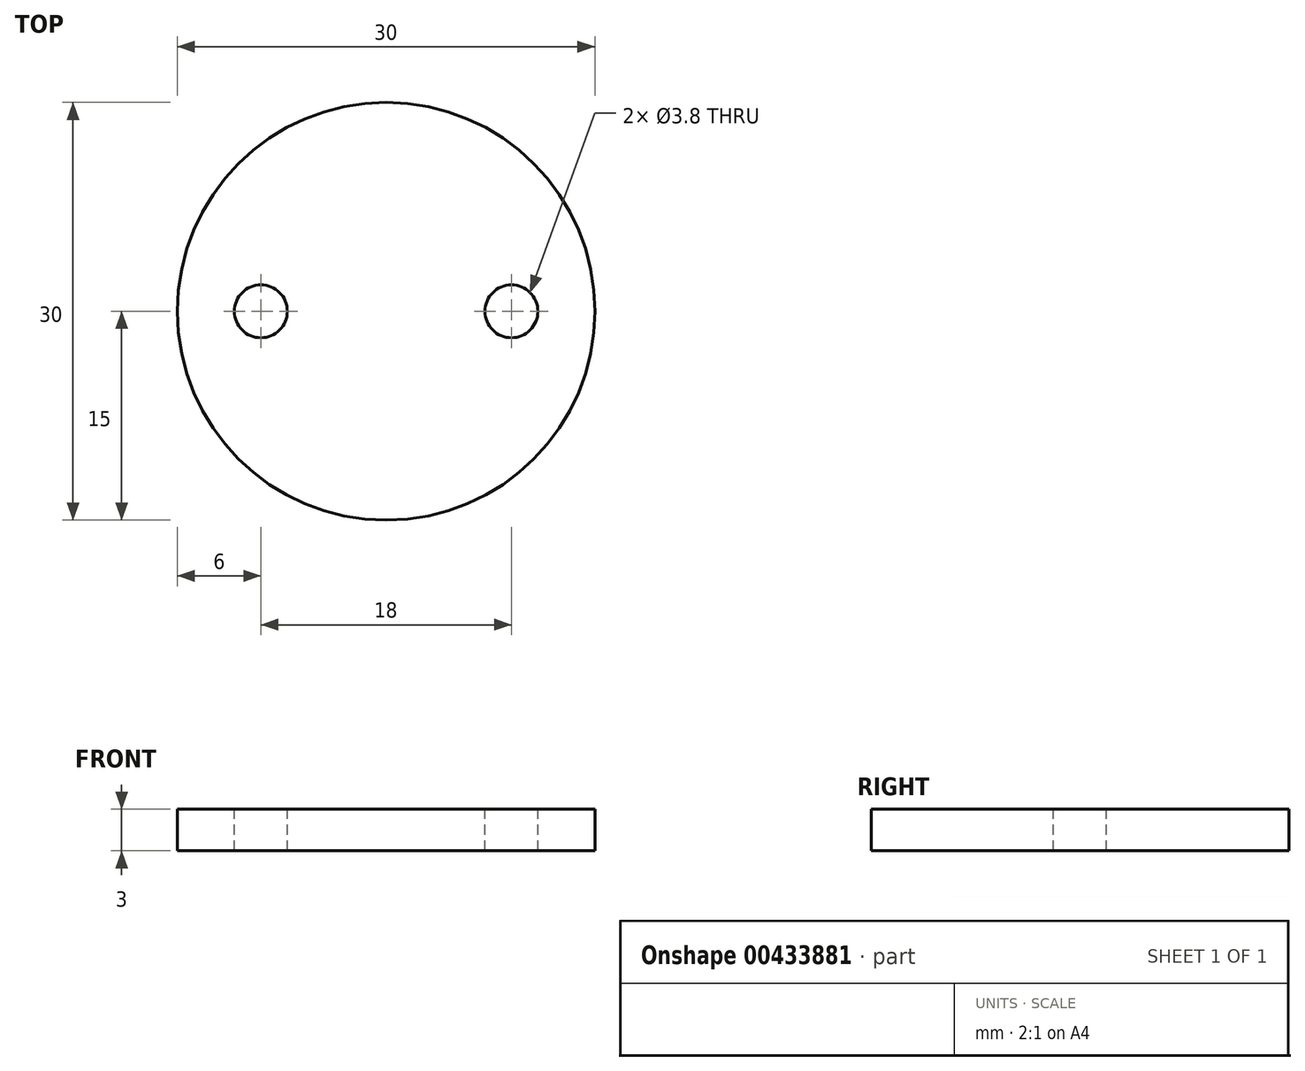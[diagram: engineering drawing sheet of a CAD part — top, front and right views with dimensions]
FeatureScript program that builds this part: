
annotation { "Feature Type Name" : "Feature", "Feature Type Description" : "" }
export const myFeature = defineFeature(function(context is Context, id is Id, definition is map)
    precondition{}
    {
        {
            var Q0;
            Q0=qCreatedBy(makeId("Top.planeOp"),FACE);
            var sketch = newSketch(context, id + "F0", { "sketchPlane" : qUnion([Q0])});
            skCircle(sketch, "E0", {"center": v(0, 0) * mm, "radius": 15 * mm});
            skSolve(sketch);
        }
        {
            var Q0;
            Q0=makeQuery(id+"F0.imprint","IMPRINT",FACE,{"disambiguationData":[TD([[makeQuery(id+"F0.imprint","IMPRINT",EDGE,{"derivedFrom":sQuery(id+"F0.wireOp",EDGE,"E0")}),1.0]])]});
            extrude(context, id + "F1", {"entities" : qUnion([Q0]), "depth" : 3 * mm});
        }
        {
            var Q0;
            Q0=makeQuery(id+"F1.opExtrude","CAP_FACE",FACE,{"disambiguationData":[OSD([sQuery(id+"F0.wireOp",EDGE,"E0")])],"isStart":false});
            var sketch = newSketch(context, id + "F2", { "sketchPlane" : qUnion([Q0])});
            skCircle(sketch, "E1", {"center": v(9, 0) * mm, "radius": 1.9 * mm});
            skCircle(sketch, "E2", {"center": v(-9, 0) * mm, "radius": 1.9 * mm});
            skSolve(sketch);
        }
        {
            var Q0;
            Q0 = qSketchRegion(id + "F2", true);
            extrude(context, id + "F3", {"entities" : qUnion([Q0]), "operationType" : NewBodyOperationType.REMOVE, "oppositeDirection" : true, "depth" : 25 * mm});
        }
    });
